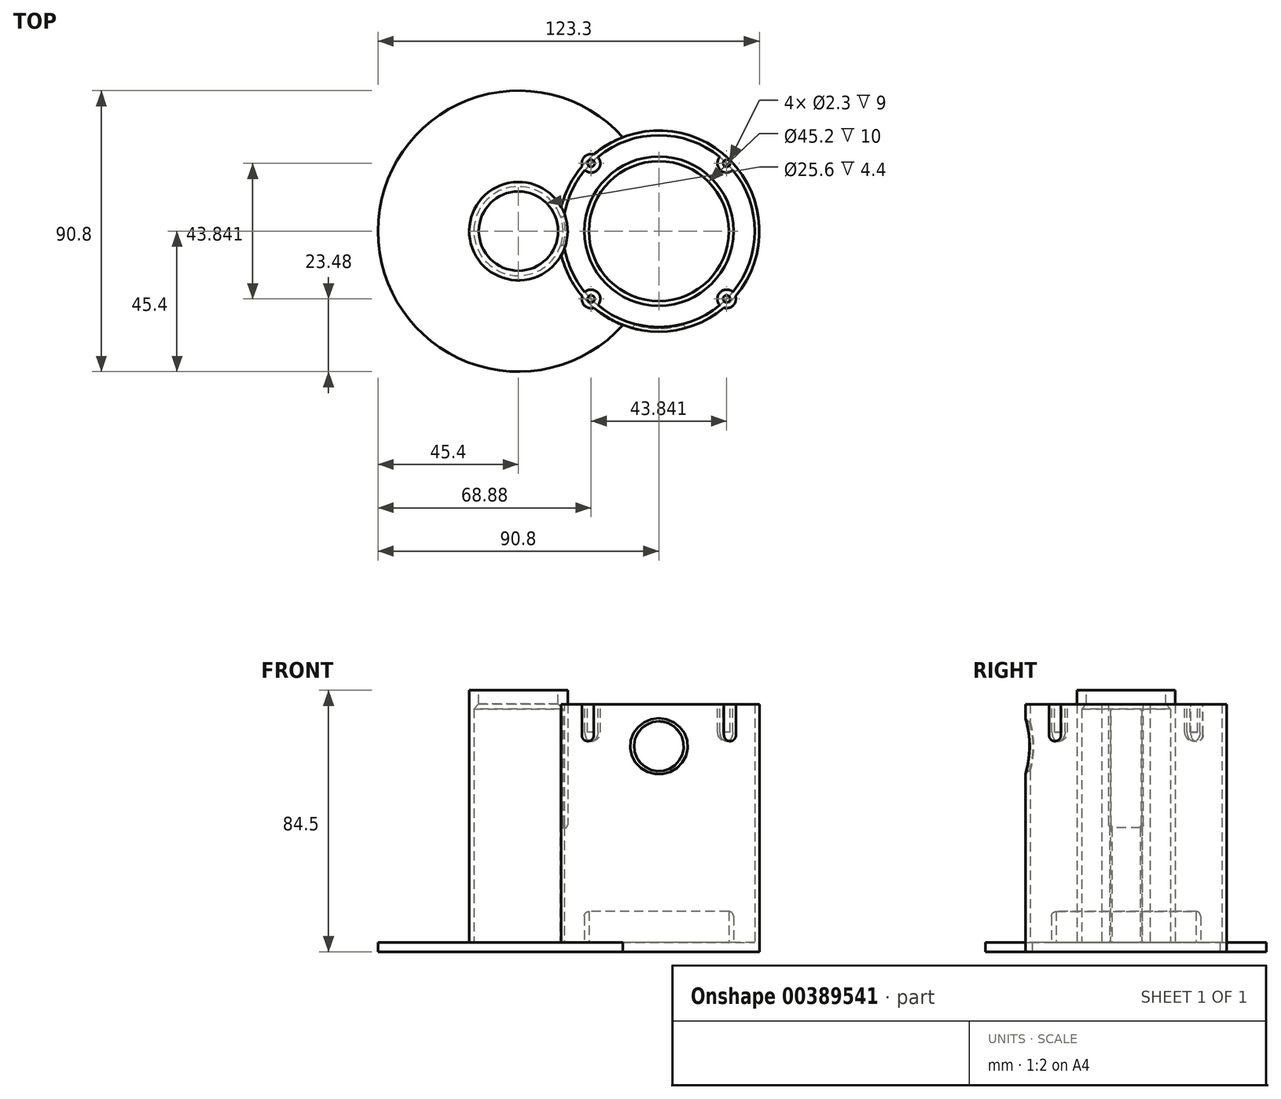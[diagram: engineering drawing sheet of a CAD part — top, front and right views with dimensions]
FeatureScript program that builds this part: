
annotation { "Feature Type Name" : "Feature", "Feature Type Description" : "" }
export const myFeature = defineFeature(function(context is Context, id is Id, definition is map)
    precondition{}
    {
        {
            var Q0;
            Q0=qCreatedBy(makeId("Top.planeOp"),FACE);
            var sketch = newSketch(context, id + "F0", { "sketchPlane" : qUnion([Q0])});
            skPoint(sketch, "E0", {"position": v(-31.55, 7.8) * mm});
            skPoint(sketch, "E1", {"position": v(-30.55, 5.25) * mm});
            skPoint(sketch, "E2", {"position": v(-31.93, 5.08) * mm});
            skPoint(sketch, "E3", {"position": v(-31.55, -7.8) * mm});
            skPoint(sketch, "E4", {"position": v(-30.55, -5.26) * mm});
            skPoint(sketch, "E5", {"position": v(-31.94, -5.12) * mm});
            skArc(sketch, "E6", {"start": v(-31.55, -7.8) * mm, "mid": v(32.5, 0) * mm, "end": v(-31.55, 7.8) * mm});
            skArc(sketch, "E7", {"start": v(-31.55, 7.8) * mm, "mid": v(-61.3, 0) * mm, "end": v(-31.55, -7.8) * mm});
            skArc(sketch, "E8", {"start": v(-31.93, 5.08) * mm, "mid": v(-31.17, 4.57) * mm, "end": v(-30.55, 5.25) * mm});
            skArc(sketch, "E9", {"start": v(-30.55, -5.26) * mm, "mid": v(-31.18, -4.54) * mm, "end": v(-31.94, -5.12) * mm});
            skArc(sketch, "E10", {"start": v(-30.55, -5.26) * mm, "mid": v(31, 0) * mm, "end": v(-30.55, 5.25) * mm});
            skArc(sketch, "E11", {"start": v(-31.93, 5.08) * mm, "mid": v(-59.8, 0.02) * mm, "end": v(-31.94, -5.12) * mm});
            skSolve(sketch);
        }
        {
            var Q0;
            Q0=makeQuery(id+"F0.imprint","IMPRINT",FACE,{"disambiguationData":[TD([[makeQuery(id+"F0.imprint","IMPRINT",EDGE,{"derivedFrom":sQuery(id+"F0.wireOp",EDGE,"E6")}),1.0]])]});
            extrude(context, id + "F1", {"entities" : qUnion([Q0]), "depth" : 80 * mm});
        }
        {
            var Q0;
            Q0=qCreatedBy(makeId("Top.planeOp"),FACE);
            var sketch = newSketch(context, id + "F2", { "sketchPlane" : qUnion([Q0])});
            skCircle(sketch, "E12", {"center": v(0, 0) * mm, "radius": 32.5 * mm});
            skCircle(sketch, "E13", {"center": v(-45.4, 0) * mm, "radius": 15.9 * mm});
            skPoint(sketch, "E14", {"position": v(-31.55, 7.8) * mm});
            skPoint(sketch, "E15", {"position": v(-31.55, -7.8) * mm});
            skSolve(sketch);
        }
        {
            var Q0;
            {var subQ0=sQuery(id+"F2.wireOp",EDGE,"E13");var subQ1=sQuery(id+"F2.wireOp",EDGE,"E12");var subQ2=makeQuery(id+"F2.imprint","INTERSECT",VERTEX,{"disambiguationData":[OD(0.0)],"derivedFrom":[subQ1,subQ0]});Q0=makeQuery(id+"F2.imprint","IMPRINT",FACE,{"disambiguationData":[TD([[makeQuery(id+"F2.imprint","IMPRINT",EDGE,{"disambiguationData":[TD([[subQ2,-1.0]])],"derivedFrom":subQ1}),1.0]])]});}
            var Q1;
            {var subQ0=sQuery(id+"F2.wireOp",EDGE,"E13");var subQ1=sQuery(id+"F2.wireOp",EDGE,"E12");var subQ2=makeQuery(id+"F2.imprint","INTERSECT",VERTEX,{"disambiguationData":[OD(0.0)],"derivedFrom":[subQ1,subQ0]});Q1=makeQuery(id+"F2.imprint","IMPRINT",FACE,{"disambiguationData":[TD([[makeQuery(id+"F2.imprint","IMPRINT",EDGE,{"disambiguationData":[TD([[subQ2,1.0]])],"derivedFrom":subQ1}),-1.0]])]});}
            var Q2;
            {var subQ0=sQuery(id+"F2.wireOp",EDGE,"E13");var subQ1=sQuery(id+"F2.wireOp",EDGE,"E12");var subQ2=makeQuery(id+"F2.imprint","INTERSECT",VERTEX,{"disambiguationData":[OD(0.0)],"derivedFrom":[subQ1,subQ0]});Q2=makeQuery(id+"F2.imprint","IMPRINT",FACE,{"disambiguationData":[TD([[makeQuery(id+"F2.imprint","IMPRINT",EDGE,{"disambiguationData":[TD([[subQ2,1.0]])],"derivedFrom":subQ1}),1.0]])]});}
            extrude(context, id + "F3", {"entities" : qUnion([Q0, Q1, Q2]), "operationType" : NewBodyOperationType.ADD, "depth" : 3 * mm});
        }
        {
            var Q0;
            Q0=makeQuery(id+"F3.opExtrude","CAP_FACE",FACE,{"disambiguationData":[OSD([sQuery(id+"F2.wireOp",EDGE,"E12"),sQuery(id+"F2.wireOp",EDGE,"E13")])],"isStart":false});
            var sketch = newSketch(context, id + "F4", { "sketchPlane" : qUnion([Q0])});
            skCircle(sketch, "E16", {"center": v(0, 0) * mm, "radius": 22.6 * mm});
            skCircle(sketch, "E17", {"center": v(0, 0) * mm, "radius": 24.1 * mm});
            skSolve(sketch);
        }
        {
            var Q0;
            Q0=makeQuery(id+"F4.imprint","IMPRINT",FACE,{"disambiguationData":[TD([[makeQuery(id+"F4.imprint","IMPRINT",EDGE,{"derivedFrom":sQuery(id+"F4.wireOp",EDGE,"E16")}),-1.0]])]});
            extrude(context, id + "F5", {"entities" : qUnion([Q0]), "operationType" : NewBodyOperationType.ADD, "depth" : 10 * mm});
        }
        {
            var Q0;
            Q0=makeQuery(id+"F1.opExtrude","CAP_FACE",FACE,{"disambiguationData":[OSD([sQuery(id+"F0.wireOp",EDGE,"E6"),sQuery(id+"F0.wireOp",EDGE,"E7"),sQuery(id+"F0.wireOp",EDGE,"E8"),sQuery(id+"F0.wireOp",EDGE,"E9"),sQuery(id+"F0.wireOp",EDGE,"E10"),sQuery(id+"F0.wireOp",EDGE,"E11")])],"isStart":false});
            var sketch = newSketch(context, id + "F6", { "sketchPlane" : qUnion([Q0])});
            skPoint(sketch, "E18", {"position": v(0, 0) * mm});
            skPoint(sketch, "E19", {"position": v(-45.4, 0) * mm});
            skCircle(sketch, "E20", {"center": v(-45.4, 0) * mm, "radius": 15.9 * mm});
            skCircle(sketch, "E21", {"center": v(-45.4, 0) * mm, "radius": 14.4 * mm});
            skSolve(sketch);
        }
        {
            var Q0;
            {var subQ0=makeQuery(id+"F1.opExtrude","CAP_EDGE",EDGE,{"disambiguationData":[OSD([sQuery(id+"F0.wireOp",EDGE,"E10")])],"isStart":false});var subQ8=sQuery(id+"F6.wireOp",EDGE,"E20");var subQ9=makeQuery(id+"F6.imprint","INTERSECT",VERTEX,{"disambiguationData":[OD(0.0)],"derivedFrom":[subQ0,subQ8]});Q0=makeQuery(id+"F6.imprint","IMPRINT",FACE,{"disambiguationData":[TD([[makeQuery(id+"F6.imprint","IMPRINT",EDGE,{"disambiguationData":[TD([[subQ9,1.0]])],"derivedFrom":subQ8}),1.0]])]});}
            extrude(context, id + "F7", {"entities" : qUnion([Q0]), "operationType" : NewBodyOperationType.ADD, "depth" : -40 * mm});
        }
        {
            var Q0;
            Q0=qCreatedBy(makeId("Front.planeOp"),FACE);
            var sketch = newSketch(context, id + "F8", { "sketchPlane" : qUnion([Q0])});
            skLineSegment(sketch, "E22", {"start": v(0, 0) * mm, "end": v(0, 80.04) * mm});
            skCircle(sketch, "E23", {"center": v(0, 66.42) * mm, "radius": 8.03 * mm});
            skSolve(sketch);
        }
        {
            var Q0;
            {var subQ0=sQuery(id+"F8.wireOp",EDGE,"E23");var subQ1=sQuery(id+"F8.wireOp",EDGE,"E22");var subQ2=makeQuery(id+"F8.imprint","INTERSECT",VERTEX,{"disambiguationData":[OD(0.0)],"derivedFrom":[subQ1,subQ0]});Q0=makeQuery(id+"F8.imprint","IMPRINT",FACE,{"disambiguationData":[TD([[makeQuery(id+"F8.imprint","IMPRINT",EDGE,{"disambiguationData":[TD([[subQ2,-1.0]])],"derivedFrom":subQ1}),-1.0]])]});}
            var Q1;
            {var subQ0=sQuery(id+"F8.wireOp",EDGE,"E23");var subQ1=sQuery(id+"F8.wireOp",EDGE,"E22");var subQ2=makeQuery(id+"F8.imprint","INTERSECT",VERTEX,{"disambiguationData":[OD(0.0)],"derivedFrom":[subQ1,subQ0]});Q1=makeQuery(id+"F8.imprint","IMPRINT",FACE,{"disambiguationData":[TD([[makeQuery(id+"F8.imprint","IMPRINT",EDGE,{"disambiguationData":[TD([[subQ2,-1.0]])],"derivedFrom":subQ1}),1.0]])]});}
            extrude(context, id + "F9", {"entities" : qUnion([Q0, Q1]), "operationType" : NewBodyOperationType.REMOVE, "oppositeDirection" : true, "depth" : -40 * mm});
        }
        {
            var Q0;
            Q0=makeQuery(id+"F5.opExtrude","CAP_EDGE",EDGE,{"disambiguationData":[OSD([sQuery(id+"F4.wireOp",EDGE,"E17")])],"isStart":false});
            fillet(context, id + "F10", {"entities" : qUnion([Q0]), "radius" : 1.5 * mm, "tangentPropagation" : true, "allowEdgeOverflow" : false});
        }
        {
            var Q0;
            Q0=makeQuery(id+"F9.boolean.opBoolean","INTERSECT",EDGE,{"derivedFrom":[makeQuery(id+"F1.opExtrude","SWEPT_FACE",FACE,{"disambiguationData":[OSD([sQuery(id+"F0.wireOp",EDGE,"E6")])]}),makeQuery(id+"F9.opExtrude","SWEPT_FACE",FACE,{"disambiguationData":[OSD([sQuery(id+"F8.wireOp",EDGE,"E23")])]})]});
            fillet(context, id + "F11", {"entities" : qUnion([Q0]), "radius" : 1 * mm, "tangentPropagation" : true, "allowEdgeOverflow" : false});
        }
        {
            var Q0;
            Q0=makeQuery(id+"F7.opExtrude","CAP_EDGE",EDGE,{"disambiguationData":[OSD([sQuery(id+"F6.wireOp",EDGE,"E20")])],"isStart":false});
            var Q1;
            Q1=makeQuery(id+"F7.opExtrude","CAP_EDGE",EDGE,{"disambiguationData":[OSD([sQuery(id+"F6.wireOp",EDGE,"E21")])],"isStart":false});
            fillet(context, id + "F12", {"entities" : qUnion([Q0, Q1]), "radius" : 1 * mm, "tangentPropagation" : true, "allowEdgeOverflow" : false});
        }
        {
            var Q0;
            {var subQ0=sQuery(id+"F0.wireOp",EDGE,"E10");var subQ1=sQuery(id+"F0.wireOp",EDGE,"E9");var subQ2=sQuery(id+"F0.wireOp",EDGE,"E8");Q0=makeQuery(id+"F7.boolean.opBoolean","MERGE",FACE,{"derivedFrom":[makeQuery(id+"F1.opExtrude","CAP_FACE",FACE,{"disambiguationData":[OSD([sQuery(id+"F0.wireOp",EDGE,"E6"),sQuery(id+"F0.wireOp",EDGE,"E7"),subQ2,subQ1,subQ0,sQuery(id+"F0.wireOp",EDGE,"E11")])],"isStart":false}),makeQuery(id+"F7.opExtrude","CAP_FACE",FACE,{"disambiguationData":[OSD([subQ2,subQ1,subQ0,sQuery(id+"F6.wireOp",EDGE,"E20"),sQuery(id+"F6.wireOp",EDGE,"E21")])],"isStart":true})]});}
            var sketch = newSketch(context, id + "F13", { "sketchPlane" : qUnion([Q0])});
            skPoint(sketch, "E24", {"position": v(-45.4, 0) * mm});
            skCircle(sketch, "E25", {"center": v(-45.4, 0) * mm, "radius": 15.9 * mm});
            skSolve(sketch);
        }
        {
            var Q0;
            Q0=makeQuery(id+"F13.imprint","IMPRINT",FACE,{"disambiguationData":[TD([[makeQuery(id+"F13.imprint","IMPRINT",EDGE,{"derivedFrom":makeQuery(id+"F1.opExtrude","CAP_EDGE",EDGE,{"disambiguationData":[OSD([sQuery(id+"F0.wireOp",EDGE,"E11")])],"isStart":false})}),-1.0]])]});
            var Q1;
            Q1=makeQuery(id+"F13.imprint","IMPRINT",FACE,{"disambiguationData":[TD([[makeQuery(id+"F13.imprint","IMPRINT",EDGE,{"derivedFrom":makeQuery(id+"F1.opExtrude","CAP_EDGE",EDGE,{"disambiguationData":[OSD([sQuery(id+"F0.wireOp",EDGE,"E11")])],"isStart":false})}),1.0]])]});
            extrude(context, id + "F14", {"entities" : qUnion([Q0, Q1]), "operationType" : NewBodyOperationType.ADD, "endBound" : BoundingType.SYMMETRIC, "depth" : 3 * mm});
        }
        {
            var Q0;
            Q0=makeQuery(id+"F14.opExtrude","CAP_FACE",FACE,{"disambiguationData":[OSD([sQuery(id+"F13.wireOp",EDGE,"E25")])],"isStart":false});
            var sketch = newSketch(context, id + "F15", { "sketchPlane" : qUnion([Q0])});
            skPoint(sketch, "E26", {"position": v(-45.4, 0) * mm});
            skCircle(sketch, "E27", {"center": v(-45.4, 0) * mm, "radius": 12.8 * mm});
            skSolve(sketch);
        }
        {
            var Q0;
            Q0=makeQuery(id+"F15.imprint","IMPRINT",FACE,{"disambiguationData":[TD([[makeQuery(id+"F15.imprint","IMPRINT",EDGE,{"derivedFrom":sQuery(id+"F15.wireOp",EDGE,"E27")}),1.0]])]});
            extrude(context, id + "F16", {"entities" : qUnion([Q0]), "operationType" : NewBodyOperationType.REMOVE, "oppositeDirection" : true, "depth" : 25 * mm});
        }
        {
            var Q0;
            {var subQ0=sQuery(id+"F0.wireOp",EDGE,"E10");var subQ1=sQuery(id+"F0.wireOp",EDGE,"E9");var subQ2=sQuery(id+"F0.wireOp",EDGE,"E8");Q0=makeQuery(id+"F7.boolean.opBoolean","MERGE",FACE,{"derivedFrom":[makeQuery(id+"F1.opExtrude","CAP_FACE",FACE,{"disambiguationData":[OSD([sQuery(id+"F0.wireOp",EDGE,"E6"),sQuery(id+"F0.wireOp",EDGE,"E7"),subQ2,subQ1,subQ0,sQuery(id+"F0.wireOp",EDGE,"E11")])],"isStart":false}),makeQuery(id+"F7.opExtrude","CAP_FACE",FACE,{"disambiguationData":[OSD([subQ2,subQ1,subQ0,sQuery(id+"F6.wireOp",EDGE,"E20"),sQuery(id+"F6.wireOp",EDGE,"E21")])],"isStart":true})]});}
            var sketch = newSketch(context, id + "F17", { "sketchPlane" : qUnion([Q0])});
            skCircle(sketch, "E28", {"center": v(0, 0) * mm, "radius": 32.5 * mm});
            skPoint(sketch, "E29", {"position": v(-22.98, 22.98) * mm});
            skPoint(sketch, "E30", {"position": v(22.98, 22.98) * mm});
            skPoint(sketch, "E31", {"position": v(22.98, -22.98) * mm});
            skPoint(sketch, "E32", {"position": v(-22.98, -22.98) * mm});
            skPoint(sketch, "E33", {"position": v(-21.92, -21.92) * mm});
            skPoint(sketch, "E34", {"position": v(-21.92, 21.92) * mm});
            skPoint(sketch, "E35", {"position": v(21.92, 21.92) * mm});
            skPoint(sketch, "E36", {"position": v(21.9, -21.9) * mm});
            skCircle(sketch, "E37", {"center": v(21.92, 21.92) * mm, "radius": 3 * mm});
            skCircle(sketch, "E38", {"center": v(-21.92, 21.92) * mm, "radius": 3 * mm});
            skCircle(sketch, "E39", {"center": v(-21.92, -21.92) * mm, "radius": 3 * mm});
            skCircle(sketch, "E40", {"center": v(21.9, -21.9) * mm, "radius": 3 * mm});
            skSolve(sketch);
        }
        {
            var Q0;
            Q0=qCreatedBy(makeId("Top.planeOp"),FACE);
            var sketch = newSketch(context, id + "F18", { "sketchPlane" : qUnion([Q0])});
            skPoint(sketch, "E41", {"position": v(-45.4, 0) * mm});
            skCircle(sketch, "E42", {"center": v(-45.4, 0) * mm, "radius": 45.4 * mm});
            skSolve(sketch);
        }
        {
            var Q0;
            Q0=makeQuery(id+"F18.imprint","IMPRINT",FACE,{"disambiguationData":[TD([[makeQuery(id+"F18.imprint","IMPRINT",EDGE,{"derivedFrom":sQuery(id+"F18.wireOp",EDGE,"E42")}),1.0]])]});
            extrude(context, id + "F19", {"entities" : qUnion([Q0]), "operationType" : NewBodyOperationType.ADD, "depth" : 3 * mm});
        }
        {
            var Q0;
            {var subQ0=sQuery(id+"F17.wireOp",EDGE,"E38");var subQ1=makeQuery(id+"F1.opExtrude","CAP_EDGE",EDGE,{"disambiguationData":[OSD([sQuery(id+"F0.wireOp",EDGE,"E10")])],"isStart":false});var subQ2=makeQuery(id+"F17.imprint","INTERSECT",VERTEX,{"disambiguationData":[OD(0.0)],"derivedFrom":[subQ1,subQ0]});Q0=makeQuery(id+"F17.imprint","IMPRINT",FACE,{"disambiguationData":[TD([[makeQuery(id+"F17.imprint","IMPRINT",EDGE,{"disambiguationData":[TD([[subQ2,1.0]])],"derivedFrom":subQ0}),1.0]])]});}
            var Q1;
            {var subQ0=sQuery(id+"F17.wireOp",EDGE,"E37");var subQ1=makeQuery(id+"F1.opExtrude","CAP_EDGE",EDGE,{"disambiguationData":[OSD([sQuery(id+"F0.wireOp",EDGE,"E10")])],"isStart":false});var subQ2=makeQuery(id+"F17.imprint","INTERSECT",VERTEX,{"disambiguationData":[OD(0.0)],"derivedFrom":[subQ1,subQ0]});Q1=makeQuery(id+"F17.imprint","IMPRINT",FACE,{"disambiguationData":[TD([[makeQuery(id+"F17.imprint","IMPRINT",EDGE,{"disambiguationData":[TD([[subQ2,-1.0]])],"derivedFrom":subQ0}),1.0]])]});}
            var Q2;
            {var subQ0=sQuery(id+"F17.wireOp",EDGE,"E40");var subQ1=makeQuery(id+"F1.opExtrude","CAP_EDGE",EDGE,{"disambiguationData":[OSD([sQuery(id+"F0.wireOp",EDGE,"E10")])],"isStart":false});var subQ2=makeQuery(id+"F17.imprint","INTERSECT",VERTEX,{"disambiguationData":[OD(0.0)],"derivedFrom":[subQ1,subQ0]});Q2=makeQuery(id+"F17.imprint","IMPRINT",FACE,{"disambiguationData":[TD([[makeQuery(id+"F17.imprint","IMPRINT",EDGE,{"disambiguationData":[TD([[subQ2,-1.0]])],"derivedFrom":subQ0}),1.0]])]});}
            var Q3;
            {var subQ0=sQuery(id+"F17.wireOp",EDGE,"E39");var subQ1=makeQuery(id+"F1.opExtrude","CAP_EDGE",EDGE,{"disambiguationData":[OSD([sQuery(id+"F0.wireOp",EDGE,"E10")])],"isStart":false});var subQ2=makeQuery(id+"F17.imprint","INTERSECT",VERTEX,{"disambiguationData":[OD(0.0)],"derivedFrom":[subQ1,subQ0]});Q3=makeQuery(id+"F17.imprint","IMPRINT",FACE,{"disambiguationData":[TD([[makeQuery(id+"F17.imprint","IMPRINT",EDGE,{"disambiguationData":[TD([[subQ2,1.0]])],"derivedFrom":subQ0}),1.0]])]});}
            var Q4;
            {var subQ0=sQuery(id+"F17.wireOp",EDGE,"E40");var subQ1=sQuery(id+"F17.wireOp",EDGE,"E28");var subQ2=makeQuery(id+"F17.imprint","INTERSECT",VERTEX,{"disambiguationData":[OD(0.0)],"derivedFrom":[subQ1,subQ0]});Q4=makeQuery(id+"F17.imprint","IMPRINT",FACE,{"disambiguationData":[TD([[makeQuery(id+"F17.imprint","IMPRINT",EDGE,{"disambiguationData":[TD([[subQ2,-1.0]])],"derivedFrom":subQ1}),-1.0]])]});}
            var Q5;
            {var subQ0=sQuery(id+"F17.wireOp",EDGE,"E40");var subQ1=sQuery(id+"F17.wireOp",EDGE,"E28");var subQ2=makeQuery(id+"F17.imprint","INTERSECT",VERTEX,{"disambiguationData":[OD(0.0)],"derivedFrom":[subQ1,subQ0]});Q5=makeQuery(id+"F17.imprint","IMPRINT",FACE,{"disambiguationData":[TD([[makeQuery(id+"F17.imprint","IMPRINT",EDGE,{"disambiguationData":[TD([[subQ2,-1.0]])],"derivedFrom":subQ1}),1.0]])]});}
            var Q6;
            {var subQ0=sQuery(id+"F17.wireOp",EDGE,"E39");var subQ1=sQuery(id+"F17.wireOp",EDGE,"E28");var subQ2=makeQuery(id+"F17.imprint","INTERSECT",VERTEX,{"disambiguationData":[OD(0.0)],"derivedFrom":[subQ1,subQ0]});Q6=makeQuery(id+"F17.imprint","IMPRINT",FACE,{"disambiguationData":[TD([[makeQuery(id+"F17.imprint","IMPRINT",EDGE,{"disambiguationData":[TD([[subQ2,-1.0]])],"derivedFrom":subQ1}),-1.0]])]});}
            var Q7;
            {var subQ0=sQuery(id+"F17.wireOp",EDGE,"E39");var subQ1=sQuery(id+"F17.wireOp",EDGE,"E28");var subQ2=makeQuery(id+"F17.imprint","INTERSECT",VERTEX,{"disambiguationData":[OD(0.0)],"derivedFrom":[subQ1,subQ0]});Q7=makeQuery(id+"F17.imprint","IMPRINT",FACE,{"disambiguationData":[TD([[makeQuery(id+"F17.imprint","IMPRINT",EDGE,{"disambiguationData":[TD([[subQ2,-1.0]])],"derivedFrom":subQ1}),1.0]])]});}
            var Q8;
            {var subQ0=sQuery(id+"F17.wireOp",EDGE,"E38");var subQ1=sQuery(id+"F17.wireOp",EDGE,"E28");var subQ2=makeQuery(id+"F17.imprint","INTERSECT",VERTEX,{"disambiguationData":[OD(0.0)],"derivedFrom":[subQ1,subQ0]});Q8=makeQuery(id+"F17.imprint","IMPRINT",FACE,{"disambiguationData":[TD([[makeQuery(id+"F17.imprint","IMPRINT",EDGE,{"disambiguationData":[TD([[subQ2,-1.0]])],"derivedFrom":subQ1}),-1.0]])]});}
            var Q9;
            {var subQ0=sQuery(id+"F17.wireOp",EDGE,"E38");var subQ1=sQuery(id+"F17.wireOp",EDGE,"E28");var subQ2=makeQuery(id+"F17.imprint","INTERSECT",VERTEX,{"disambiguationData":[OD(0.0)],"derivedFrom":[subQ1,subQ0]});Q9=makeQuery(id+"F17.imprint","IMPRINT",FACE,{"disambiguationData":[TD([[makeQuery(id+"F17.imprint","IMPRINT",EDGE,{"disambiguationData":[TD([[subQ2,-1.0]])],"derivedFrom":subQ1}),1.0]])]});}
            var Q10;
            {var subQ0=sQuery(id+"F17.wireOp",EDGE,"E37");var subQ1=sQuery(id+"F17.wireOp",EDGE,"E28");var subQ2=makeQuery(id+"F17.imprint","INTERSECT",VERTEX,{"disambiguationData":[OD(0.0)],"derivedFrom":[subQ1,subQ0]});Q10=makeQuery(id+"F17.imprint","IMPRINT",FACE,{"disambiguationData":[TD([[makeQuery(id+"F17.imprint","IMPRINT",EDGE,{"disambiguationData":[TD([[subQ2,-1.0]])],"derivedFrom":subQ1}),-1.0]])]});}
            var Q11;
            {var subQ0=sQuery(id+"F17.wireOp",EDGE,"E37");var subQ1=sQuery(id+"F17.wireOp",EDGE,"E28");var subQ2=makeQuery(id+"F17.imprint","INTERSECT",VERTEX,{"disambiguationData":[OD(0.0)],"derivedFrom":[subQ1,subQ0]});Q11=makeQuery(id+"F17.imprint","IMPRINT",FACE,{"disambiguationData":[TD([[makeQuery(id+"F17.imprint","IMPRINT",EDGE,{"disambiguationData":[TD([[subQ2,-1.0]])],"derivedFrom":subQ1}),1.0]])]});}
            extrude(context, id + "F20", {"entities" : qUnion([Q0, Q1, Q2, Q3, Q4, Q5, Q6, Q7, Q8, Q9, Q10, Q11]), "operationType" : NewBodyOperationType.ADD, "depth" : -12 * mm});
        }
        {
            var Q0;
            {var subQ0=sQuery(id+"F17.wireOp",EDGE,"E38");Q0=makeQuery(id+"F20.boolean.opBoolean","SPLIT",EDGE,{"disambiguationData":[TD([makeQuery(id+"F1.opExtrude","SWEPT_FACE",FACE,{"disambiguationData":[OSD([sQuery(id+"F0.wireOp",EDGE,"E10")])]})])],"derivedFrom":makeQuery(id+"F20.opExtrude","CAP_EDGE",EDGE,{"disambiguationData":[OSD([subQ0])],"isStart":false})});}
            var Q1;
            {var subQ0=sQuery(id+"F17.wireOp",EDGE,"E39");Q1=makeQuery(id+"F20.boolean.opBoolean","SPLIT",EDGE,{"disambiguationData":[TD([makeQuery(id+"F1.opExtrude","SWEPT_FACE",FACE,{"disambiguationData":[OSD([sQuery(id+"F0.wireOp",EDGE,"E10")])]})])],"derivedFrom":makeQuery(id+"F20.opExtrude","CAP_EDGE",EDGE,{"disambiguationData":[OSD([subQ0])],"isStart":false})});}
            var Q2;
            {var subQ0=sQuery(id+"F17.wireOp",EDGE,"E37");Q2=makeQuery(id+"F20.boolean.opBoolean","SPLIT",EDGE,{"disambiguationData":[TD([makeQuery(id+"F1.opExtrude","SWEPT_FACE",FACE,{"disambiguationData":[OSD([sQuery(id+"F0.wireOp",EDGE,"E10")])]})])],"derivedFrom":makeQuery(id+"F20.opExtrude","CAP_EDGE",EDGE,{"disambiguationData":[OSD([subQ0])],"isStart":false})});}
            var Q3;
            {var subQ0=sQuery(id+"F17.wireOp",EDGE,"E40");Q3=makeQuery(id+"F20.boolean.opBoolean","SPLIT",EDGE,{"disambiguationData":[TD([makeQuery(id+"F1.opExtrude","SWEPT_FACE",FACE,{"disambiguationData":[OSD([sQuery(id+"F0.wireOp",EDGE,"E10")])]})])],"derivedFrom":makeQuery(id+"F20.opExtrude","CAP_EDGE",EDGE,{"disambiguationData":[OSD([subQ0])],"isStart":false})});}
            fillet(context, id + "F21", {"entities" : qUnion([Q0, Q1, Q2, Q3]), "radius" : 3 * mm, "tangentPropagation" : true, "allowEdgeOverflow" : false});
        }
        {
            var Q0;
            {var subQ0=sQuery(id+"F17.wireOp",EDGE,"E37");Q0=makeQuery(id+"F20.boolean.opBoolean","SPLIT",EDGE,{"disambiguationData":[TD([makeQuery(id+"F1.opExtrude","SWEPT_FACE",FACE,{"disambiguationData":[OSD([sQuery(id+"F0.wireOp",EDGE,"E6")])]})])],"derivedFrom":makeQuery(id+"F20.opExtrude","CAP_EDGE",EDGE,{"disambiguationData":[OSD([subQ0])],"isStart":false})});}
            var Q1;
            {var subQ0=sQuery(id+"F17.wireOp",EDGE,"E38");Q1=makeQuery(id+"F20.boolean.opBoolean","SPLIT",EDGE,{"disambiguationData":[TD([makeQuery(id+"F1.opExtrude","SWEPT_FACE",FACE,{"disambiguationData":[OSD([sQuery(id+"F0.wireOp",EDGE,"E6")])]})])],"derivedFrom":makeQuery(id+"F20.opExtrude","CAP_EDGE",EDGE,{"disambiguationData":[OSD([subQ0])],"isStart":false})});}
            var Q2;
            {var subQ0=sQuery(id+"F17.wireOp",EDGE,"E40");Q2=makeQuery(id+"F20.boolean.opBoolean","SPLIT",EDGE,{"disambiguationData":[TD([makeQuery(id+"F1.opExtrude","SWEPT_FACE",FACE,{"disambiguationData":[OSD([sQuery(id+"F0.wireOp",EDGE,"E6")])]})])],"derivedFrom":makeQuery(id+"F20.opExtrude","CAP_EDGE",EDGE,{"disambiguationData":[OSD([subQ0])],"isStart":false})});}
            var Q3;
            {var subQ0=sQuery(id+"F17.wireOp",EDGE,"E39");Q3=makeQuery(id+"F20.boolean.opBoolean","SPLIT",EDGE,{"disambiguationData":[TD([makeQuery(id+"F1.opExtrude","SWEPT_FACE",FACE,{"disambiguationData":[OSD([sQuery(id+"F0.wireOp",EDGE,"E6")])]})])],"derivedFrom":makeQuery(id+"F20.opExtrude","CAP_EDGE",EDGE,{"disambiguationData":[OSD([subQ0])],"isStart":false})});}
            fillet(context, id + "F22", {"entities" : qUnion([Q0, Q1, Q2, Q3]), "radius" : 2 * mm, "tangentPropagation" : true, "allowEdgeOverflow" : false});
        }
        {
            var Q0;
            {var subQ0=sQuery(id+"F0.wireOp",EDGE,"E10");var subQ1=sQuery(id+"F0.wireOp",EDGE,"E9");var subQ2=sQuery(id+"F0.wireOp",EDGE,"E8");Q0=makeQuery(id+"F20.boolean.opBoolean","MERGE",FACE,{"derivedFrom":[makeQuery(id+"F7.boolean.opBoolean","MERGE",FACE,{"derivedFrom":[makeQuery(id+"F1.opExtrude","CAP_FACE",FACE,{"disambiguationData":[OSD([sQuery(id+"F0.wireOp",EDGE,"E6"),sQuery(id+"F0.wireOp",EDGE,"E7"),subQ2,subQ1,subQ0,sQuery(id+"F0.wireOp",EDGE,"E11")])],"isStart":false}),makeQuery(id+"F7.opExtrude","CAP_FACE",FACE,{"disambiguationData":[OSD([subQ2,subQ1,subQ0,sQuery(id+"F6.wireOp",EDGE,"E20"),sQuery(id+"F6.wireOp",EDGE,"E21")])],"isStart":true})]}),makeQuery(id+"F20.opExtrude","CAP_FACE",FACE,{"disambiguationData":[OSD([sQuery(id+"F17.wireOp",EDGE,"E37")])],"isStart":true}),makeQuery(id+"F20.opExtrude","CAP_FACE",FACE,{"disambiguationData":[OSD([sQuery(id+"F17.wireOp",EDGE,"E38")])],"isStart":true}),makeQuery(id+"F20.opExtrude","CAP_FACE",FACE,{"disambiguationData":[OSD([sQuery(id+"F17.wireOp",EDGE,"E39")])],"isStart":true}),makeQuery(id+"F20.opExtrude","CAP_FACE",FACE,{"disambiguationData":[OSD([sQuery(id+"F17.wireOp",EDGE,"E40")])],"isStart":true})]});}
            var sketch = newSketch(context, id + "F23", { "sketchPlane" : qUnion([Q0])});
            skPoint(sketch, "E43", {"position": v(-21.92, -21.92) * mm});
            skPoint(sketch, "E44", {"position": v(21.9, -21.9) * mm});
            skPoint(sketch, "E45", {"position": v(21.92, 21.92) * mm});
            skPoint(sketch, "E46", {"position": v(-21.92, 21.92) * mm});
            skCircle(sketch, "E47", {"center": v(-21.92, -21.92) * mm, "radius": 1.15 * mm});
            skCircle(sketch, "E48", {"center": v(-21.92, 21.92) * mm, "radius": 1.15 * mm});
            skCircle(sketch, "E49", {"center": v(21.9, -21.9) * mm, "radius": 1.15 * mm});
            skCircle(sketch, "E50", {"center": v(21.92, 21.92) * mm, "radius": 1.15 * mm});
            skSolve(sketch);
        }
        {
            var Q0;
            Q0=makeQuery(id+"F23.imprint","IMPRINT",FACE,{"disambiguationData":[TD([[makeQuery(id+"F23.imprint","IMPRINT",EDGE,{"derivedFrom":sQuery(id+"F23.wireOp",EDGE,"E47")}),1.0]])]});
            var Q1;
            Q1=makeQuery(id+"F23.imprint","IMPRINT",FACE,{"disambiguationData":[TD([[makeQuery(id+"F23.imprint","IMPRINT",EDGE,{"derivedFrom":sQuery(id+"F23.wireOp",EDGE,"E49")}),1.0]])]});
            var Q2;
            Q2=makeQuery(id+"F23.imprint","IMPRINT",FACE,{"disambiguationData":[TD([[makeQuery(id+"F23.imprint","IMPRINT",EDGE,{"derivedFrom":sQuery(id+"F23.wireOp",EDGE,"E50")}),1.0]])]});
            var Q3;
            Q3=makeQuery(id+"F23.imprint","IMPRINT",FACE,{"disambiguationData":[TD([[makeQuery(id+"F23.imprint","IMPRINT",EDGE,{"derivedFrom":sQuery(id+"F23.wireOp",EDGE,"E48")}),1.0]])]});
            extrude(context, id + "F24", {"entities" : qUnion([Q0, Q1, Q2, Q3]), "operationType" : NewBodyOperationType.REMOVE, "depth" : -9 * mm});
        }
        {
            var Q0;
            Q0=makeQuery(id+"F16.boolean.opBoolean","INTERSECT",EDGE,{"derivedFrom":[makeQuery(id+"F14.opExtrude","CAP_FACE",FACE,{"disambiguationData":[OSD([sQuery(id+"F13.wireOp",EDGE,"E25")])],"isStart":true}),makeQuery(id+"F16.opExtrude","SWEPT_FACE",FACE,{"disambiguationData":[OSD([sQuery(id+"F15.wireOp",EDGE,"E27")])]})]});
            chamfer(context, id + "F25", {"entities" : qUnion([Q0]), "width" : 1.6 * mm, "tangentPropagation" : true});
        }
        {
            var Q0;
            Q0=makeQuery(id+"F14.opExtrude","CAP_FACE",FACE,{"disambiguationData":[OSD([sQuery(id+"F13.wireOp",EDGE,"E25")])],"isStart":false});
            extrude(context, id + "F26", {"entities" : qUnion([Q0]), "operationType" : NewBodyOperationType.ADD, "depth" : 3 * mm});
        }
    });
